# Revit family: Plymold-Essentials-Industrial_Bench_Unit
name_source: partatom
category: Furniture
units: mm (PartAtom-declared; Revit-internal decimal feet)

## family parameters
Always vertical = Yes
Cut with Voids When Loaded = No
OmniClass Number = 23.40.20.00
OmniClass Title = General Furniture and Specialties
Render Appearance Source = Family Geometry
Room Calculation Point = No
Shared = No
Work Plane-Based = No

## types (3) — shared parameters
Assembly Code = E2020200
Brand = Island Bench Units
CAP MATERIAL = PLY - Plastic Black
Default Elevation = 0"
Depth = 57"
EDGE MATERIAL = PLY - Plastic Black
FRAME MATERIAL = PLY - Onyx Black Powdercoat
GLIDES MATERIAL = PLY - Plastic Black
Height = 30"
Keynote = 12500
LEG MATERIAL = PLY - Onyx Black Powdercoat
Manufacturer = Plymold
Product Documentation Link = https://plymold.com
Revit Model Built By = https://www.servex-us.com
SEAT MATERIAL = PLY - Wood Mahogany - Horizontal
Sustainability = https://plymold.com
TOP EDGE MATERIAL = PLY - Plastic Black
TOP MATERIAL = PLY - Wood Mahogany - Horizontal
Type Comments = Cafeteria Seating
URL = https://plymold.com
zero-valued in all types: Cost

## per-type parameters (varying)
| type | Description | Width |
| IDBE048VE | Industrial Bench Unit - 48”W x 57”D x 30”H | 48" |
| IDBE072VE | Industrial Bench Unit - 72”W x 57”D x 30”H | 72" |
| IDBE096VE | Industrial Bench Unit - 96”W x 57”D x 30”H | 96" |

note: column(s) folded — value = type name in every type: Model

## geometry (parser evidence)
native form markers: Sweep x7
no freeform markers — native parametric forms only
